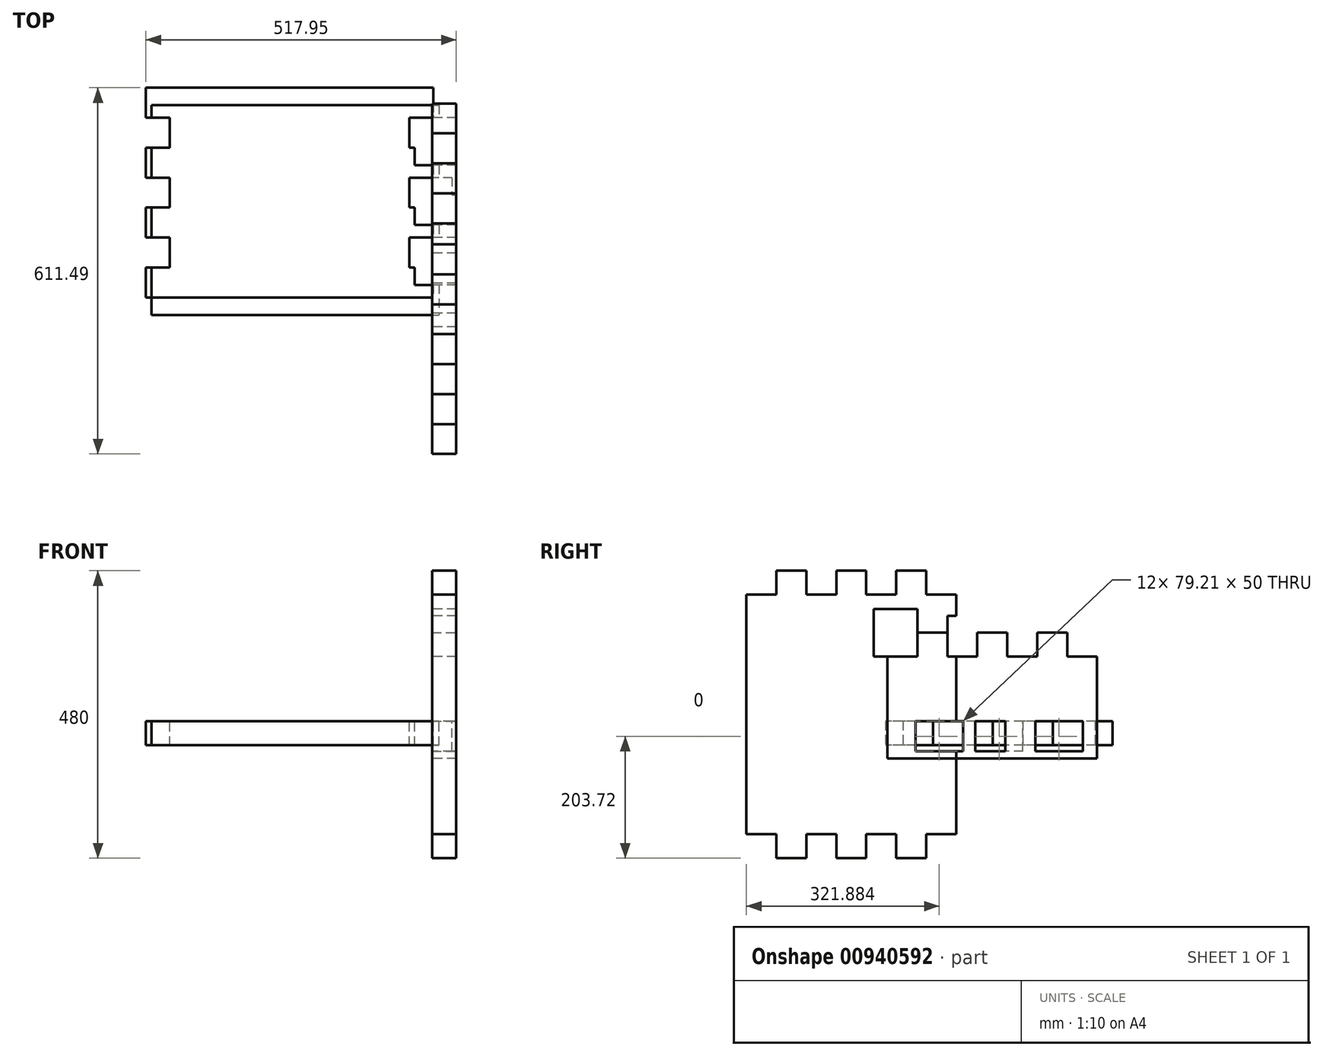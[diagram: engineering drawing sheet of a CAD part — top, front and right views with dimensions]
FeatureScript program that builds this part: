
annotation { "Feature Type Name" : "Feature", "Feature Type Description" : "" }
export const myFeature = defineFeature(function(context is Context, id is Id, definition is map)
    precondition{}
    {
        {
            var Q0;
            Q0=qCreatedBy(makeId("Top.planeOp"),FACE);
            var sketch = newSketch(context, id + "F0", { "sketchPlane" : qUnion([Q0])});
            skLineSegment(sketch, "E0.bottom", {"start": v(-468.88, 312.17) * mm, "end": v(11.12, 312.17) * mm});
            skLineSegment(sketch, "E0.top", {"start": v(-468.88, -37.83) * mm, "end": v(11.12, -37.83) * mm});
            skLineSegment(sketch, "E0.left", {"start": v(-468.88, 312.17) * mm, "end": v(-468.88, -37.83) * mm});
            skLineSegment(sketch, "E0.right", {"start": v(11.12, 312.17) * mm, "end": v(11.12, -37.83) * mm});
            skSolve(sketch);
        }
        {
            var Q0;
            Q0 = qSketchRegion(id + "F0", true);
            extrude(context, id + "F1", {"entities" : qUnion([Q0]), "depth" : 40 * mm, "offsetDistance" : 25 * mm});
        }
        {
            var Q0;
            Q0=qCreatedBy(makeId("Right.planeOp"),FACE);
            var sketch = newSketch(context, id + "F2", { "sketchPlane" : qUnion([Q0])});
            skLineSegment(sketch, "E1.bottom", {"start": v(-270.11, 291.28) * mm, "end": v(79.89, 291.28) * mm});
            skLineSegment(sketch, "E1.top", {"start": v(-270.11, -188.72) * mm, "end": v(79.89, -188.72) * mm});
            skLineSegment(sketch, "E1.left", {"start": v(-270.11, 291.28) * mm, "end": v(-270.11, -188.72) * mm});
            skLineSegment(sketch, "E1.right", {"start": v(79.89, 291.28) * mm, "end": v(79.89, -188.72) * mm});
            skSolve(sketch);
        }
        {
            var Q0;
            Q0 = qSketchRegion(id + "F2", true);
            extrude(context, id + "F3", {"entities" : qUnion([Q0]), "depth" : 40 * mm, "offsetDistance" : 25 * mm});
        }
        {
            var Q0;
            Q0=qCreatedBy(makeId("Top.planeOp"),FACE);
            var sketch = newSketch(context, id + "F4", { "sketchPlane" : qUnion([Q0])});
            skLineSegment(sketch, "E2.bottom", {"start": v(-477.95, 341.38) * mm, "end": v(2.05, 341.38) * mm});
            skLineSegment(sketch, "E2.top", {"start": v(-477.95, -8.62) * mm, "end": v(2.05, -8.62) * mm});
            skLineSegment(sketch, "E2.left", {"start": v(-477.95, 341.38) * mm, "end": v(-477.95, -8.62) * mm});
            skLineSegment(sketch, "E2.right", {"start": v(2.05, 341.38) * mm, "end": v(2.05, -8.62) * mm});
            skSolve(sketch);
        }
        {
            var Q0;
            Q0 = qSketchRegion(id + "F4", true);
            extrude(context, id + "F5", {"entities" : qUnion([Q0]), "depth" : 40 * mm, "offsetDistance" : 25 * mm});
        }
        {
            var Q0;
            Q0=qCreatedBy(makeId("Right.planeOp"),FACE);
            var sketch = newSketch(context, id + "F6", { "sketchPlane" : qUnion([Q0])});
            skLineSegment(sketch, "E3.bottom", {"start": v(315.25, 188.14) * mm, "end": v(-34.75, 188.14) * mm});
            skLineSegment(sketch, "E3.top", {"start": v(315.25, -21.86) * mm, "end": v(-34.75, -21.86) * mm});
            skLineSegment(sketch, "E3.left", {"start": v(315.25, 188.14) * mm, "end": v(315.25, -21.86) * mm});
            skLineSegment(sketch, "E3.right", {"start": v(-34.75, 188.14) * mm, "end": v(-34.75, -21.86) * mm});
            skSolve(sketch);
        }
        {
            var Q0;
            Q0 = qSketchRegion(id + "F6", true);
            extrude(context, id + "F7", {"entities" : qUnion([Q0]), "depth" : 40 * mm, "offsetDistance" : 25 * mm});
        }
        {
            var Q0;
            Q0=makeQuery(id+"F1.opExtrude","CAP_FACE",FACE,{"disambiguationData":[OSD([sQuery(id+"F0.wireOp",EDGE,"E0.bottom"),sQuery(id+"F0.wireOp",EDGE,"E0.top"),sQuery(id+"F0.wireOp",EDGE,"E0.left"),sQuery(id+"F0.wireOp",EDGE,"E0.right")])],"isStart":false});
            var sketch = newSketch(context, id + "F8", { "sketchPlane" : qUnion([Q0])});
            skLineSegment(sketch, "E4.bottom", {"start": v(56.15, 12.17) * mm, "end": v(-28.88, 12.17) * mm});
            skLineSegment(sketch, "E4.top", {"start": v(56.15, 62.17) * mm, "end": v(-28.88, 62.17) * mm});
            skLineSegment(sketch, "E4.left", {"start": v(56.15, 12.17) * mm, "end": v(56.15, 62.17) * mm});
            skLineSegment(sketch, "E4.right", {"start": v(-28.88, 12.17) * mm, "end": v(-28.88, 62.17) * mm});
            skLineSegment(sketch, "E5.bottom", {"start": v(57.3, 112.17) * mm, "end": v(-28.88, 112.17) * mm});
            skLineSegment(sketch, "E5.top", {"start": v(57.3, 162.17) * mm, "end": v(-28.88, 162.17) * mm});
            skLineSegment(sketch, "E5.left", {"start": v(57.3, 112.17) * mm, "end": v(57.3, 162.17) * mm});
            skLineSegment(sketch, "E5.right", {"start": v(-28.88, 112.17) * mm, "end": v(-28.88, 162.17) * mm});
            skLineSegment(sketch, "E6.bottom", {"start": v(87.76, 212.17) * mm, "end": v(-28.88, 212.17) * mm});
            skLineSegment(sketch, "E6.top", {"start": v(87.76, 262.17) * mm, "end": v(-28.88, 262.17) * mm});
            skLineSegment(sketch, "E6.left", {"start": v(87.76, 212.17) * mm, "end": v(87.76, 262.17) * mm});
            skLineSegment(sketch, "E6.right", {"start": v(-28.88, 212.17) * mm, "end": v(-28.88, 262.17) * mm});
            skSolve(sketch);
        }
        {
            var Q0;
            Q0 = qSketchRegion(id + "F8", true);
            extrude(context, id + "F9", {"entities" : qUnion([Q0]), "operationType" : NewBodyOperationType.REMOVE, "oppositeDirection" : true, "depth" : 50 * mm, "offsetDistance" : 25 * mm});
        }
        {
            var Q0;
            Q0=makeQuery(id+"F3.opExtrude","CAP_FACE",FACE,{"disambiguationData":[OSD([sQuery(id+"F2.wireOp",EDGE,"E1.bottom"),sQuery(id+"F2.wireOp",EDGE,"E1.top"),sQuery(id+"F2.wireOp",EDGE,"E1.left"),sQuery(id+"F2.wireOp",EDGE,"E1.right")])],"isStart":true});
            var sketch = newSketch(context, id + "F10", { "sketchPlane" : qUnion([Q0])});
            skLineSegment(sketch, "E7.bottom", {"start": v(-104.53, 348.95) * mm, "end": v(-29.89, 348.95) * mm});
            skLineSegment(sketch, "E7.top", {"start": v(-104.53, 251.28) * mm, "end": v(-29.89, 251.28) * mm});
            skLineSegment(sketch, "E7.left", {"start": v(-104.53, 348.95) * mm, "end": v(-104.53, 251.28) * mm});
            skLineSegment(sketch, "E7.right", {"start": v(-29.89, 348.95) * mm, "end": v(-29.89, 251.28) * mm});
            skLineSegment(sketch, "E8.bottom", {"start": v(20.11, 362.23) * mm, "end": v(70.11, 362.23) * mm});
            skLineSegment(sketch, "E8.top", {"start": v(20.11, 251.28) * mm, "end": v(70.11, 251.28) * mm});
            skLineSegment(sketch, "E8.left", {"start": v(20.11, 362.23) * mm, "end": v(20.11, 251.28) * mm});
            skLineSegment(sketch, "E8.right", {"start": v(70.11, 362.23) * mm, "end": v(70.11, 251.28) * mm});
            skLineSegment(sketch, "E9.bottom", {"start": v(120.11, 362.23) * mm, "end": v(170.11, 362.23) * mm});
            skLineSegment(sketch, "E9.top", {"start": v(120.11, 251.28) * mm, "end": v(170.11, 251.28) * mm});
            skLineSegment(sketch, "E9.left", {"start": v(120.11, 362.23) * mm, "end": v(120.11, 251.28) * mm});
            skLineSegment(sketch, "E9.right", {"start": v(170.11, 362.23) * mm, "end": v(170.11, 251.28) * mm});
            skLineSegment(sketch, "E10.bottom", {"start": v(220.11, 331.28) * mm, "end": v(287.61, 331.28) * mm});
            skLineSegment(sketch, "E10.top", {"start": v(220.11, 251.28) * mm, "end": v(287.61, 251.28) * mm});
            skLineSegment(sketch, "E10.left", {"start": v(220.11, 331.28) * mm, "end": v(220.11, 251.28) * mm});
            skLineSegment(sketch, "E10.right", {"start": v(287.61, 331.28) * mm, "end": v(287.61, 251.28) * mm});
            skLineSegment(sketch, "E11.bottom", {"start": v(-93.41, -148.72) * mm, "end": v(-29.89, -148.72) * mm});
            skLineSegment(sketch, "E11.top", {"start": v(-93.41, -250.37) * mm, "end": v(-29.89, -250.37) * mm});
            skLineSegment(sketch, "E11.left", {"start": v(-93.41, -148.72) * mm, "end": v(-93.41, -250.37) * mm});
            skLineSegment(sketch, "E11.right", {"start": v(-29.89, -148.72) * mm, "end": v(-29.89, -250.37) * mm});
            skLineSegment(sketch, "E12.bottom", {"start": v(20.11, -148.72) * mm, "end": v(70.11, -148.72) * mm});
            skLineSegment(sketch, "E12.top", {"start": v(20.11, -276.89) * mm, "end": v(70.11, -276.89) * mm});
            skLineSegment(sketch, "E12.left", {"start": v(20.11, -148.72) * mm, "end": v(20.11, -276.89) * mm});
            skLineSegment(sketch, "E12.right", {"start": v(70.11, -148.72) * mm, "end": v(70.11, -276.89) * mm});
            skLineSegment(sketch, "E13.bottom", {"start": v(120.11, -148.72) * mm, "end": v(170.11, -148.72) * mm});
            skLineSegment(sketch, "E13.top", {"start": v(120.11, -263.39) * mm, "end": v(170.11, -263.39) * mm});
            skLineSegment(sketch, "E13.left", {"start": v(120.11, -148.72) * mm, "end": v(120.11, -263.39) * mm});
            skLineSegment(sketch, "E13.right", {"start": v(170.11, -148.72) * mm, "end": v(170.11, -263.39) * mm});
            skLineSegment(sketch, "E14.bottom", {"start": v(220.11, -148.72) * mm, "end": v(305.08, -148.72) * mm});
            skLineSegment(sketch, "E14.top", {"start": v(220.11, -274.5) * mm, "end": v(305.08, -274.5) * mm});
            skLineSegment(sketch, "E14.left", {"start": v(220.11, -148.72) * mm, "end": v(220.11, -274.5) * mm});
            skLineSegment(sketch, "E14.right", {"start": v(305.08, -148.72) * mm, "end": v(305.08, -274.5) * mm});
            skSolve(sketch);
        }
        {
            var Q0;
            Q0 = qSketchRegion(id + "F10", true);
            extrude(context, id + "F11", {"entities" : qUnion([Q0]), "operationType" : NewBodyOperationType.REMOVE, "oppositeDirection" : true, "depth" : 100 * mm, "offsetDistance" : 25 * mm});
        }
        {
            var Q0;
            Q0=makeQuery(id+"F5.opExtrude","CAP_FACE",FACE,{"disambiguationData":[OSD([sQuery(id+"F4.wireOp",EDGE,"E2.bottom"),sQuery(id+"F4.wireOp",EDGE,"E2.top"),sQuery(id+"F4.wireOp",EDGE,"E2.left"),sQuery(id+"F4.wireOp",EDGE,"E2.right")])],"isStart":false});
            var sketch = newSketch(context, id + "F12", { "sketchPlane" : qUnion([Q0])});
            skLineSegment(sketch, "E15.bottom", {"start": v(-516.31, 291.38) * mm, "end": v(-437.95, 291.38) * mm});
            skLineSegment(sketch, "E15.top", {"start": v(-516.31, 241.38) * mm, "end": v(-437.95, 241.38) * mm});
            skLineSegment(sketch, "E15.left", {"start": v(-516.31, 291.38) * mm, "end": v(-516.31, 241.38) * mm});
            skLineSegment(sketch, "E15.right", {"start": v(-437.95, 291.38) * mm, "end": v(-437.95, 241.38) * mm});
            skLineSegment(sketch, "E16.bottom", {"start": v(-493.64, 191.38) * mm, "end": v(-437.95, 191.38) * mm});
            skLineSegment(sketch, "E16.top", {"start": v(-493.64, 141.38) * mm, "end": v(-437.95, 141.38) * mm});
            skLineSegment(sketch, "E16.left", {"start": v(-493.64, 191.38) * mm, "end": v(-493.64, 141.38) * mm});
            skLineSegment(sketch, "E16.right", {"start": v(-437.95, 191.38) * mm, "end": v(-437.95, 141.38) * mm});
            skLineSegment(sketch, "E17.bottom", {"start": v(-508.57, 91.38) * mm, "end": v(-437.95, 91.38) * mm});
            skLineSegment(sketch, "E17.top", {"start": v(-508.57, 41.38) * mm, "end": v(-437.95, 41.38) * mm});
            skLineSegment(sketch, "E17.left", {"start": v(-508.57, 91.38) * mm, "end": v(-508.57, 41.38) * mm});
            skLineSegment(sketch, "E17.right", {"start": v(-437.95, 91.38) * mm, "end": v(-437.95, 41.38) * mm});
            skLineSegment(sketch, "E18.bottom", {"start": v(42.22, 291.38) * mm, "end": v(-37.95, 291.38) * mm});
            skLineSegment(sketch, "E18.top", {"start": v(42.22, 241.38) * mm, "end": v(-37.95, 241.38) * mm});
            skLineSegment(sketch, "E18.left", {"start": v(42.22, 291.38) * mm, "end": v(42.22, 241.38) * mm});
            skLineSegment(sketch, "E18.right", {"start": v(-37.95, 291.38) * mm, "end": v(-37.95, 241.38) * mm});
            skLineSegment(sketch, "E19.bottom", {"start": v(33.13, 191.38) * mm, "end": v(-37.95, 191.38) * mm});
            skLineSegment(sketch, "E19.top", {"start": v(33.13, 141.38) * mm, "end": v(-37.95, 141.38) * mm});
            skLineSegment(sketch, "E19.left", {"start": v(33.13, 191.38) * mm, "end": v(33.13, 141.38) * mm});
            skLineSegment(sketch, "E19.right", {"start": v(-37.95, 191.38) * mm, "end": v(-37.95, 141.38) * mm});
            skLineSegment(sketch, "E20.bottom", {"start": v(40.7, 91.38) * mm, "end": v(-37.95, 91.38) * mm});
            skLineSegment(sketch, "E20.top", {"start": v(40.7, 41.38) * mm, "end": v(-37.95, 41.38) * mm});
            skLineSegment(sketch, "E20.left", {"start": v(40.7, 91.38) * mm, "end": v(40.7, 41.38) * mm});
            skLineSegment(sketch, "E20.right", {"start": v(-37.95, 91.38) * mm, "end": v(-37.95, 41.38) * mm});
            skSolve(sketch);
        }
        {
            var Q0;
            Q0 = qSketchRegion(id + "F12", true);
            extrude(context, id + "F13", {"entities" : qUnion([Q0]), "operationType" : NewBodyOperationType.REMOVE, "oppositeDirection" : true, "depth" : 50 * mm, "offsetDistance" : 25 * mm});
        }
        {
            var Q0;
            Q0=makeQuery(id+"F7.opExtrude","CAP_FACE",FACE,{"disambiguationData":[OSD([sQuery(id+"F6.wireOp",EDGE,"E3.bottom"),sQuery(id+"F6.wireOp",EDGE,"E3.top"),sQuery(id+"F6.wireOp",EDGE,"E3.left"),sQuery(id+"F6.wireOp",EDGE,"E3.right")])],"isStart":true});
            var sketch = newSketch(context, id + "F14", { "sketchPlane" : qUnion([Q0])});
            skLineSegment(sketch, "E21.bottom", {"start": v(-265.25, 238.5) * mm, "end": v(-339.56, 238.5) * mm});
            skLineSegment(sketch, "E21.top", {"start": v(-265.25, 148.14) * mm, "end": v(-339.56, 148.14) * mm});
            skLineSegment(sketch, "E21.left", {"start": v(-265.25, 238.5) * mm, "end": v(-265.25, 148.14) * mm});
            skLineSegment(sketch, "E21.right", {"start": v(-339.56, 238.5) * mm, "end": v(-339.56, 148.14) * mm});
            skLineSegment(sketch, "E22.bottom", {"start": v(-215.25, 213.13) * mm, "end": v(-165.25, 213.13) * mm});
            skLineSegment(sketch, "E22.top", {"start": v(-215.25, 148.14) * mm, "end": v(-165.25, 148.14) * mm});
            skLineSegment(sketch, "E22.left", {"start": v(-215.25, 213.13) * mm, "end": v(-215.25, 148.14) * mm});
            skLineSegment(sketch, "E22.right", {"start": v(-165.25, 213.13) * mm, "end": v(-165.25, 148.14) * mm});
            skLineSegment(sketch, "E23.bottom", {"start": v(-115.25, 215.8) * mm, "end": v(-65.25, 215.8) * mm});
            skLineSegment(sketch, "E23.top", {"start": v(-115.25, 148.14) * mm, "end": v(-65.25, 148.14) * mm});
            skLineSegment(sketch, "E23.left", {"start": v(-115.25, 215.8) * mm, "end": v(-115.25, 148.14) * mm});
            skLineSegment(sketch, "E23.right", {"start": v(-65.25, 215.8) * mm, "end": v(-65.25, 148.14) * mm});
            skLineSegment(sketch, "E24.bottom", {"start": v(-15.25, 227.19) * mm, "end": v(57.72, 227.19) * mm});
            skLineSegment(sketch, "E24.top", {"start": v(-15.25, 148.14) * mm, "end": v(57.72, 148.14) * mm});
            skLineSegment(sketch, "E24.left", {"start": v(-15.25, 227.19) * mm, "end": v(-15.25, 148.14) * mm});
            skLineSegment(sketch, "E24.right", {"start": v(57.72, 227.19) * mm, "end": v(57.72, 148.14) * mm});
            skSolve(sketch);
        }
        {
            var Q0;
            Q0 = qSketchRegion(id + "F14", true);
            extrude(context, id + "F15", {"entities" : qUnion([Q0]), "operationType" : NewBodyOperationType.REMOVE, "oppositeDirection" : true, "depth" : 50 * mm, "offsetDistance" : 25 * mm});
        }
    });
